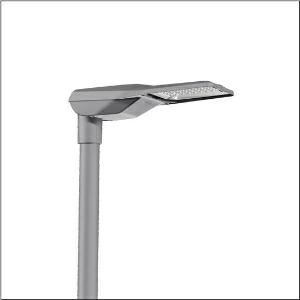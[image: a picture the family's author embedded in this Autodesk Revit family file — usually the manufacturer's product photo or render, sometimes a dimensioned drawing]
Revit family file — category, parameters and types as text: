
# Revit family: streetlight_sl_21_iq_mini___st1_0a_5xe2d21d08hb_1c5e
name_source: partatom
category: Lighting Fixtures
units: mm (PartAtom-declared; Revit-internal decimal feet)

## family parameters
Cut with Voids When Loaded = No
Host = Face
Light Source = No
Part Type = Normal
Room Calculation Point = No
Round Connector Dimension = Use Diameter
Shared = No

## types (1)
- --- (1 x LED, 7830 lm, 70.9 W, 2200K)
    Apparent Load = 71 VA
    CIE Flux Codes = 37 72 97 100 100
    Color Rendering = 70
    Color Temperature = 2200K
    Default Elevation = 1800 mm
    Description = Streetlight SL 21 iQ mini, mast luminaire, primary light control with lens, of PMMA, primary optical cover: cover, of toughened safety glass, transparent, light distribution: ST1.0a, light emission: direct distribution, primary light characteristic: asymmetric, installation type: post-top, side-entry, LED, High Power LED, rated luminous flux: 7.830lm, luminous efficacy: 110lm/W, light colour: 722, colour temperature: 2200K, control: Auto-Match, Temp-Guard, Lumen-Switch, Night-Set, Smart-Wire, Light-Fading, Desk-Remote (wireless, voltage-free reading and setting of iQ features in the workshop via application-optimized NFC function/RFID function), optimised constant luminous flux control (CLO 2.0), presetting dimming linear, mains connection: 220..240V, AC, 50/60Hz, start of lifetime: 71W, end of service life: 75W, reduction: 31W, luminaire housing, of diecast aluminium, powder-coated, Siteco® metallic grey (DB 702S), corrosivity category C5 mid according to DIN EN ISO 12944, please order mast flange separately, inclination adjustable: 0°, 5°, 10°, 15°, sealing non-destructively replaceable, multi-level sealing system, length: 628mm, width: 235mm, height: 110mm, mast flange for spigot size: 42mm (side-entry): 5XC10008XM4, 60/48mm (side-entry/post-top): 5XC10108XM2, 76/60mm (side-entry/post-top): 5XC10108XM1, protection rating (complete): IP66, insulation class (complete): insulation class II (safety insulation), certification: CE, ENEC, ENEC+, VDE, impact resistance: IK09, permissible operating ambient temperature for outdoor applications: -40..+50°C, standard-compliant lighting for roads and squares, packaging unit: 1 piece

Light Distribution: ST1.0a
    Height = 110 mm
    Lamp = 1 x LED
    Lamp Light Flux = 7830 lm
    Lamp Power = 70.9 W
    Lamp count = 1
    Length = 625 mm
    Luminous efficacy = 110 lm/W
    Manufacturer = Siteco
    ModVariant = No
    Model = 5XE2D21D08HB
    Number of Poles = 1
    OnlyDefault = Yes
    Power Factor = 1
    Product Name = Streetlight SL 21 iQ mini | ST1.0a
    Product group = mast luminaire | pylon top
    ProductGroupID = 6100
    Protection Class = Protection class II
    Protection Degree = IP 66
    RLX_Detail_Level = 1
    RLX_Emergency_Light_Flux = 0 lm
    RLX_Emergency_Type = 0
    RLX_Emergency_Type_DB = No
    RlxData = <blob elided: 92061 chars, md5=b8a518b2>
    Socket = socket
    Standby Power = 0 W
    System Light Flux = 7830 lm
    System Power = 71 W
    Type Comments = factory setting: luminous flux: 100 % | dim-lin: 254 | 711 mA
    Type Image = l_1003519.jpg
    URL = http://relux.com
    VarID = @adj_090647
    Voltage = 0 V
    Weight = 0.00 kg
    Width = 234 mm

## geometry (parser evidence)
native form markers: Blend x4, Sweep x9
no freeform markers — native parametric forms only
